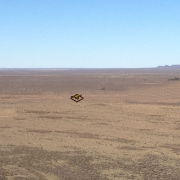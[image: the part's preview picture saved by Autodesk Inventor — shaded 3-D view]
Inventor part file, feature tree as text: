
AUTODESK INVENTOR PART (.ipt)
format: ipt  version: 2013 (Build 170138000, 138)  size: 378,880 bytes
history: native  units: in
note: dims shown in document units (in); Inventor stores cm internally (conversion verified against a paired STEP export)
features: extrude x8, sketch x8, pattern_circular x2, chamfer x1
ambient origin geometry x8: Origin, YZ Plane, XZ Plane, XY Plane, X Axis, Y Axis, Z Axis, Center Point
bodies: Solid1 (feature_tree)
feature tree (19):
  extrude  "Extrusion1"  Depth=36.0in
  chamfer  "Chamfer1"  Distance=3.937in
  extrude  "Extrusion7"  TaperAngle=30.0deg  [1 undecoded]
  extrude  "Extrusion8"  Depth=4.0in TaperAngle=0.0deg
  extrude  "Extrusion9"  Depth=300.0in
  pattern_circular  "Circular Pattern1"  Count=3 Angle=360.0deg
  extrude  "Extrusion10"  Depth=26.0in
  extrude  "Extrusion11"  Depth=18.0in
  extrude  "Extrusion12"  Depth=0.75in
  extrude  "Extrusion13"  Depth=18.0in
  pattern_circular  "Circular Pattern2"  [2 undecoded]
  sketch  "Sketch1"  dims[d0=36.0in d1=36.0in]
  sketch  "Sketch10"  dims[d2=1.9685in d3=3.937in d4=0.0in]
  sketch  "Sketch11"  dims[d10=4.0in d11=0.125in d12=45.0deg d32=30.0deg]
  sketch  "Sketch12"  dims[d33=0.987in d35=4.0in d36=0.0in]
  sketch  "Sketch13"  dims[d37=0.5in d39=300.0in]
  sketch  "Sketch14"  dims[d40=0.1in d41=0.0in]
  sketch  "Sketch15"  dims[d42=17.5in]
  sketch  "Sketch16"  dims[d44=1.0in d45=0.0in d46=1.1811in d47=360.0deg d50=26.0in d51=18.0in d53=0.75in d54=18.0in d55=0.75in d56=3.0in d57=0.0in d58=0.5in d59=1.0in d60=0.0in d61=0.5in d62=3.0in d63=0.5in d64=3.0in d65=0.5in d66=1.5in d67=1.5in d68=0.75in d69=1.0in d70=0.0in d71=0.75in d72=35.0in d73=1.0in d74=2.0in d75=0.0in d76=1.1811in d77=360.0deg]
note: 3 required parameter values undecoded (feature->parameter linkage not recoverable at this tier; creation-order binding heuristic only, values carry confidence <= 0.55)
